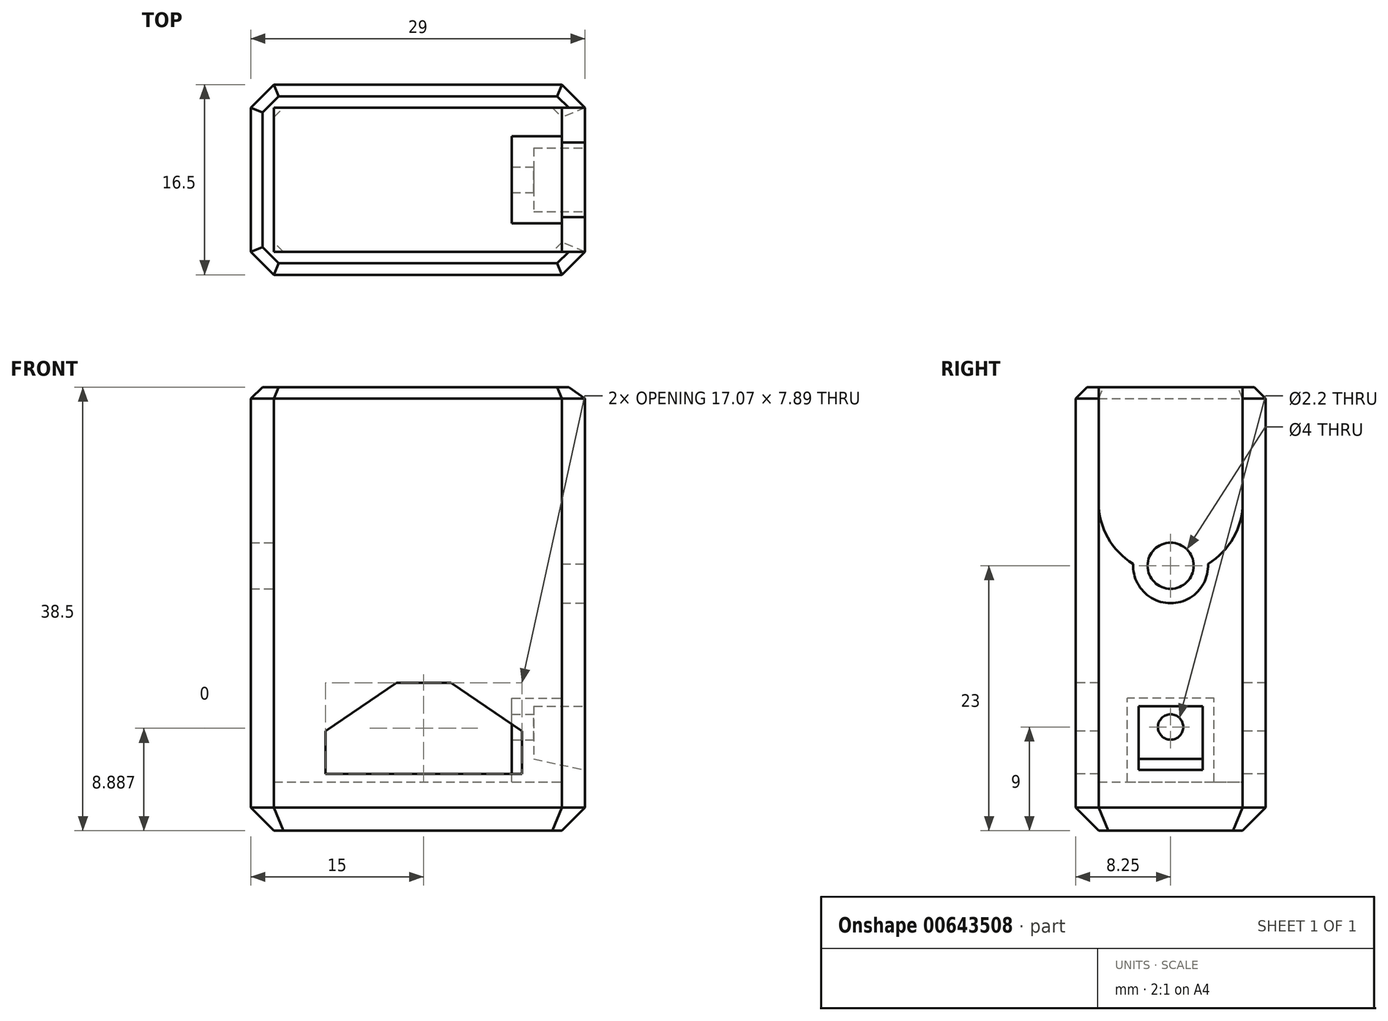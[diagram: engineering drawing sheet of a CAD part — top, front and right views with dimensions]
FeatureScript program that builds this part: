
annotation { "Feature Type Name" : "Feature", "Feature Type Description" : "" }
export const myFeature = defineFeature(function(context is Context, id is Id, definition is map)
    precondition{}
    {
        {
            var Q0;
            Q0=qCreatedBy(makeId("Top.planeOp"),FACE);
            var sketch = newSketch(context, id + "F0", { "sketchPlane" : qUnion([Q0])});
            skLineSegment(sketch, "E0.bottom", {"start": v(0, 0) * mm, "end": v(29, 0) * mm});
            skLineSegment(sketch, "E0.top", {"start": v(0, 16.5) * mm, "end": v(29, 16.5) * mm});
            skLineSegment(sketch, "E0.left", {"start": v(0, 0) * mm, "end": v(0, 16.5) * mm});
            skLineSegment(sketch, "E0.right", {"start": v(29, 0) * mm, "end": v(29, 16.5) * mm});
            skSolve(sketch);
        }
        {
            var Q0;
            Q0=qSketchRegion(id+"F0",true);
            extrude(context, id + "F1", {"entities" : qUnion([Q0]), "depth" : 38.5 * mm, "offsetDistance" : 25 * mm});
        }
        {
            var Q0;
            Q0=makeQuery(id+"F1.opExtrude","CAP_FACE",FACE,{"disambiguationData":[OSD([sQuery(id+"F0.wireOp",EDGE,"E0.bottom"),sQuery(id+"F0.wireOp",EDGE,"E0.top"),sQuery(id+"F0.wireOp",EDGE,"E0.left"),sQuery(id+"F0.wireOp",EDGE,"E0.right")])],"isStart":false});
            shell(context, id + "F2", {"entities" : qUnion([Q0]), "thickness" : 2 * mm});
        }
        {
            var Q0;
            Q0=makeQuery(id+"F2.opShell","OFFSET_FACE",FACE,{"disambiguationData":[OSD([sQuery(id+"F0.wireOp",EDGE,"E0.bottom"),sQuery(id+"F0.wireOp",EDGE,"E0.top"),sQuery(id+"F0.wireOp",EDGE,"E0.left"),sQuery(id+"F0.wireOp",EDGE,"E0.right")])]});
            extrude(context, id + "F3", {"entities" : qUnion([Q0]), "operationType" : NewBodyOperationType.ADD, "depth" : 2.25 * mm, "offsetDistance" : 25 * mm});
        }
        {
            var Q0;
            Q0=makeQuery(id+"F1.opExtrude","SWEPT_EDGE",EDGE,{"disambiguationData":[OSD([sQuery(id+"F0.wireOp",EDGE,"E0.bottom"),sQuery(id+"F0.wireOp",EDGE,"E0.right")])]});
            var Q1;
            Q1=makeQuery(id+"F1.opExtrude","SWEPT_EDGE",EDGE,{"disambiguationData":[OSD([sQuery(id+"F0.wireOp",EDGE,"E0.bottom"),sQuery(id+"F0.wireOp",EDGE,"E0.left")])]});
            var Q2;
            Q2=makeQuery(id+"F1.opExtrude","SWEPT_EDGE",EDGE,{"disambiguationData":[OSD([sQuery(id+"F0.wireOp",EDGE,"E0.top"),sQuery(id+"F0.wireOp",EDGE,"E0.right")])]});
            var Q3;
            Q3=makeQuery(id+"F1.opExtrude","SWEPT_EDGE",EDGE,{"disambiguationData":[OSD([sQuery(id+"F0.wireOp",EDGE,"E0.top"),sQuery(id+"F0.wireOp",EDGE,"E0.left")])]});
            chamfer(context, id + "F4", {"entities" : qUnion([Q0, Q1, Q2, Q3]), "width" : 2 * mm, "tangentPropagation" : true});
        }
        {
            var Q0;
            Q0=makeQuery(id+"F1.opExtrude","CAP_FACE",FACE,{"disambiguationData":[OSD([sQuery(id+"F0.wireOp",EDGE,"E0.bottom"),sQuery(id+"F0.wireOp",EDGE,"E0.top"),sQuery(id+"F0.wireOp",EDGE,"E0.left"),sQuery(id+"F0.wireOp",EDGE,"E0.right")])],"isStart":true});
            chamfer(context, id + "F5", {"entities" : qUnion([Q0]), "width" : 2 * mm, "tangentPropagation" : true});
        }
        {
            var Q0;
            Q0=makeQuery(id+"F1.opExtrude","CAP_EDGE",EDGE,{"disambiguationData":[OSD([sQuery(id+"F0.wireOp",EDGE,"E0.bottom")])],"isStart":false});
            var Q1;
            {var subQ0=sQuery(id+"F0.wireOp",EDGE,"E0.left");var subQ1=sQuery(id+"F0.wireOp",EDGE,"E0.bottom");Q1=makeQuery(id+"F4.opChamfer","BLEND_EDGE",EDGE,{"blendedFrom":[makeQuery(id+"F1.opExtrude","SWEPT_EDGE",EDGE,{"disambiguationData":[OSD([subQ1,subQ0])]}),makeQuery(id+"F1.opExtrude","CAP_FACE",FACE,{"disambiguationData":[OSD([subQ1,sQuery(id+"F0.wireOp",EDGE,"E0.top"),subQ0,sQuery(id+"F0.wireOp",EDGE,"E0.right")])],"isStart":false})],"blendedInto":[makeQuery(id+"F1.opExtrude","CAP_FACE",FACE,{"disambiguationData":[OSD([subQ1,sQuery(id+"F0.wireOp",EDGE,"E0.top"),subQ0,sQuery(id+"F0.wireOp",EDGE,"E0.right")])],"isStart":false})]});}
            var Q2;
            Q2=makeQuery(id+"F1.opExtrude","CAP_EDGE",EDGE,{"disambiguationData":[OSD([sQuery(id+"F0.wireOp",EDGE,"E0.left")])],"isStart":false});
            var Q3;
            {var subQ0=sQuery(id+"F0.wireOp",EDGE,"E0.left");var subQ1=sQuery(id+"F0.wireOp",EDGE,"E0.top");Q3=makeQuery(id+"F4.opChamfer","BLEND_EDGE",EDGE,{"blendedFrom":[makeQuery(id+"F1.opExtrude","SWEPT_EDGE",EDGE,{"disambiguationData":[OSD([subQ1,subQ0])]}),makeQuery(id+"F1.opExtrude","CAP_FACE",FACE,{"disambiguationData":[OSD([sQuery(id+"F0.wireOp",EDGE,"E0.bottom"),subQ1,subQ0,sQuery(id+"F0.wireOp",EDGE,"E0.right")])],"isStart":false})],"blendedInto":[makeQuery(id+"F1.opExtrude","CAP_FACE",FACE,{"disambiguationData":[OSD([sQuery(id+"F0.wireOp",EDGE,"E0.bottom"),subQ1,subQ0,sQuery(id+"F0.wireOp",EDGE,"E0.right")])],"isStart":false})]});}
            var Q4;
            Q4=makeQuery(id+"F1.opExtrude","CAP_EDGE",EDGE,{"disambiguationData":[OSD([sQuery(id+"F0.wireOp",EDGE,"E0.top")])],"isStart":false});
            var Q5;
            {var subQ0=sQuery(id+"F0.wireOp",EDGE,"E0.right");var subQ1=sQuery(id+"F0.wireOp",EDGE,"E0.top");Q5=makeQuery(id+"F4.opChamfer","BLEND_EDGE",EDGE,{"blendedFrom":[makeQuery(id+"F1.opExtrude","SWEPT_EDGE",EDGE,{"disambiguationData":[OSD([subQ1,subQ0])]}),makeQuery(id+"F1.opExtrude","CAP_FACE",FACE,{"disambiguationData":[OSD([sQuery(id+"F0.wireOp",EDGE,"E0.bottom"),subQ1,sQuery(id+"F0.wireOp",EDGE,"E0.left"),subQ0])],"isStart":false})],"blendedInto":[makeQuery(id+"F1.opExtrude","CAP_FACE",FACE,{"disambiguationData":[OSD([sQuery(id+"F0.wireOp",EDGE,"E0.bottom"),subQ1,sQuery(id+"F0.wireOp",EDGE,"E0.left"),subQ0])],"isStart":false})]});}
            var Q6;
            Q6=makeQuery(id+"F1.opExtrude","CAP_EDGE",EDGE,{"disambiguationData":[OSD([sQuery(id+"F0.wireOp",EDGE,"E0.right")])],"isStart":false});
            var Q7;
            {var subQ0=sQuery(id+"F0.wireOp",EDGE,"E0.right");var subQ1=sQuery(id+"F0.wireOp",EDGE,"E0.bottom");Q7=makeQuery(id+"F4.opChamfer","BLEND_EDGE",EDGE,{"blendedFrom":[makeQuery(id+"F1.opExtrude","SWEPT_EDGE",EDGE,{"disambiguationData":[OSD([subQ1,subQ0])]}),makeQuery(id+"F1.opExtrude","CAP_FACE",FACE,{"disambiguationData":[OSD([subQ1,sQuery(id+"F0.wireOp",EDGE,"E0.top"),sQuery(id+"F0.wireOp",EDGE,"E0.left"),subQ0])],"isStart":false})],"blendedInto":[makeQuery(id+"F1.opExtrude","CAP_FACE",FACE,{"disambiguationData":[OSD([subQ1,sQuery(id+"F0.wireOp",EDGE,"E0.top"),sQuery(id+"F0.wireOp",EDGE,"E0.left"),subQ0])],"isStart":false})]});}
            chamfer(context, id + "F6", {"entities" : qUnion([Q0, Q1, Q2, Q3, Q4, Q5, Q6, Q7]), "width" : 1 * mm, "tangentPropagation" : true});
        }
        {
            var Q0;
            Q0=makeQuery(id+"F1.opExtrude","SWEPT_FACE",FACE,{"disambiguationData":[OSD([sQuery(id+"F0.wireOp",EDGE,"E0.bottom")])]});
            var sketch = newSketch(context, id + "F7", { "sketchPlane" : qUnion([Q0])});
            skLineSegment(sketch, "E1", {"start": v(6.46, 4.94) * mm, "end": v(23.54, 4.94) * mm});
            skLineSegment(sketch, "E2", {"start": v(23.54, 4.94) * mm, "end": v(23.54, 8.66) * mm});
            skLineSegment(sketch, "E3", {"start": v(23.54, 8.66) * mm, "end": v(17.36, 12.83) * mm});
            skLineSegment(sketch, "E4", {"start": v(17.36, 12.83) * mm, "end": v(12.63, 12.83) * mm});
            skLineSegment(sketch, "E5", {"start": v(12.63, 12.83) * mm, "end": v(6.46, 8.66) * mm});
            skLineSegment(sketch, "E6", {"start": v(6.46, 8.66) * mm, "end": v(6.46, 4.94) * mm});
            skSolve(sketch);
        }
        {
            var Q0;
            Q0=makeQuery(id+"F7.imprint","IMPRINT",FACE,{"disambiguationData":[TD([[makeQuery(id+"F7.imprint","IMPRINT",EDGE,{"derivedFrom":sQuery(id+"F7.wireOp",EDGE,"E1")}),1.0]])]});
            extrude(context, id + "F8", {"entities" : qUnion([Q0]), "operationType" : NewBodyOperationType.REMOVE, "endBound" : BoundingType.THROUGH_ALL, "oppositeDirection" : true, "depth" : 25 * mm, "offsetDistance" : 25 * mm});
        }
        {
            var Q0;
            Q0=makeQuery(id+"F1.opExtrude","SWEPT_FACE",FACE,{"disambiguationData":[OSD([sQuery(id+"F0.wireOp",EDGE,"E0.right")])]});
            var sketch = newSketch(context, id + "F9", { "sketchPlane" : qUnion([Q0])});
            skCircle(sketch, "E7", {"center": v(8.25, 23) * mm, "radius": 3.25 * mm});
            skCircle(sketch, "E8", {"center": v(8.25, 28.5) * mm, "radius": 6.25 * mm});
            skLineSegment(sketch, "E9.bottom", {"start": v(2, 28.5) * mm, "end": v(14.5, 28.5) * mm});
            skLineSegment(sketch, "E9.top", {"start": v(2, 38.5) * mm, "end": v(14.5, 38.5) * mm});
            skLineSegment(sketch, "E9.left", {"start": v(2, 28.5) * mm, "end": v(2, 38.5) * mm});
            skLineSegment(sketch, "E9.right", {"start": v(14.5, 28.5) * mm, "end": v(14.5, 38.5) * mm});
            skSolve(sketch);
        }
        {
            var Q0;
            {var subQ0=sQuery(id+"F9.wireOp",EDGE,"E8");var subQ1=sQuery(id+"F9.wireOp",EDGE,"E7");var subQ2=makeQuery(id+"F9.imprint","INTERSECT",VERTEX,{"disambiguationData":[OD(0.0)],"derivedFrom":[subQ1,subQ0]});Q0=makeQuery(id+"F9.imprint","IMPRINT",FACE,{"disambiguationData":[TD([[makeQuery(id+"F9.imprint","IMPRINT",EDGE,{"disambiguationData":[TD([[subQ2,-1.0]])],"derivedFrom":subQ1}),1.0]])]});}
            var Q1;
            {var subQ0=sQuery(id+"F9.wireOp",EDGE,"E8");var subQ1=sQuery(id+"F9.wireOp",EDGE,"E7");var subQ2=makeQuery(id+"F9.imprint","INTERSECT",VERTEX,{"disambiguationData":[OD(0.0)],"derivedFrom":[subQ1,subQ0]});Q1=makeQuery(id+"F9.imprint","IMPRINT",FACE,{"disambiguationData":[TD([[makeQuery(id+"F9.imprint","IMPRINT",EDGE,{"disambiguationData":[TD([[subQ2,1.0]])],"derivedFrom":subQ1}),1.0]])]});}
            var Q2;
            {var subQ4=sQuery(id+"F9.wireOp",EDGE,"E9.bottom");Q2=makeQuery(id+"F9.imprint","IMPRINT",FACE,{"disambiguationData":[TD([[makeQuery(id+"F9.imprint","IMPRINT",EDGE,{"derivedFrom":subQ4}),-1.0]])]});}
            var Q3;
            {var subQ0=sQuery(id+"F9.wireOp",EDGE,"E9.bottom");Q3=makeQuery(id+"F9.imprint","IMPRINT",FACE,{"disambiguationData":[TD([[makeQuery(id+"F9.imprint","IMPRINT",EDGE,{"derivedFrom":subQ0}),1.0]])]});}
            var Q4;
            {var subQ3=sQuery(id+"F0.wireOp",EDGE,"E0.right");var subQ4=makeQuery(id+"F1.opExtrude","SWEPT_FACE",FACE,{"disambiguationData":[OSD([subQ3])]});var subQ8=makeQuery(id+"F6.opChamfer","BLEND_EDGE",EDGE,{"blendedFrom":[makeQuery(id+"F1.opExtrude","CAP_EDGE",EDGE,{"disambiguationData":[OSD([subQ3])],"isStart":false}),subQ4],"blendedInto":[subQ4]});Q4=makeQuery(id+"F9.imprint","IMPRINT",FACE,{"disambiguationData":[TD([[makeQuery(id+"F9.imprint","IMPRINT",EDGE,{"derivedFrom":subQ8}),1.0]])]});}
            var Q5;
            {var subQ0=sQuery(id+"F9.wireOp",EDGE,"E9.top");Q5=makeQuery(id+"F9.imprint","IMPRINT",FACE,{"disambiguationData":[TD([[makeQuery(id+"F9.imprint","IMPRINT",EDGE,{"derivedFrom":subQ0}),-1.0]])]});}
            extrude(context, id + "F10", {"entities" : qUnion([Q0, Q1, Q2, Q3, Q4, Q5]), "operationType" : NewBodyOperationType.REMOVE, "endBound" : BoundingType.UP_TO_NEXT, "oppositeDirection" : true, "depth" : 25 * mm, "offsetDistance" : 25 * mm});
        }
        {
            var Q0;
            Q0=makeQuery(id+"F2.opShell","OFFSET_FACE",FACE,{"disambiguationData":[OSD([sQuery(id+"F0.wireOp",EDGE,"E0.left")])]});
            var sketch = newSketch(context, id + "F11", { "sketchPlane" : qUnion([Q0])});
            skCircle(sketch, "E10", {"center": v(8.25, 23) * mm, "radius": 2 * mm});
            skSolve(sketch);
        }
        {
            var Q0;
            Q0=makeQuery(id+"F11.imprint","IMPRINT",FACE,{"disambiguationData":[TD([[makeQuery(id+"F11.imprint","IMPRINT",EDGE,{"derivedFrom":sQuery(id+"F11.wireOp",EDGE,"E10")}),1.0]])]});
            extrude(context, id + "F12", {"entities" : qUnion([Q0]), "operationType" : NewBodyOperationType.REMOVE, "endBound" : BoundingType.THROUGH_ALL, "oppositeDirection" : true, "depth" : 25 * mm, "offsetDistance" : 25 * mm});
        }
        {
            var Q0;
            Q0=makeQuery(id+"F2.opShell","OFFSET_FACE",FACE,{"disambiguationData":[OSD([sQuery(id+"F0.wireOp",EDGE,"E0.right")])]});
            var sketch = newSketch(context, id + "F13", { "sketchPlane" : qUnion([Q0])});
            skLineSegment(sketch, "E11.bottom", {"start": v(-12.02, 4.25) * mm, "end": v(-4.48, 4.25) * mm});
            skLineSegment(sketch, "E11.top", {"start": v(-12.02, 11.5) * mm, "end": v(-4.48, 11.5) * mm});
            skLineSegment(sketch, "E11.left", {"start": v(-12.02, 4.25) * mm, "end": v(-12.02, 11.5) * mm});
            skLineSegment(sketch, "E11.right", {"start": v(-4.48, 4.25) * mm, "end": v(-4.48, 11.5) * mm});
            skCircle(sketch, "E12", {"center": v(-8.25, 9) * mm, "radius": 1.1 * mm});
            skSolve(sketch);
        }
        {
            var Q0;
            Q0=qSketchRegion(id+"F13",true);
            extrude(context, id + "F14", {"entities" : qUnion([Q0]), "operationType" : NewBodyOperationType.ADD, "depth" : 4.35 * mm, "offsetDistance" : 25 * mm});
        }
        {
            var Q0;
            Q0=makeQuery(id+"F1.opExtrude","SWEPT_FACE",FACE,{"disambiguationData":[OSD([sQuery(id+"F0.wireOp",EDGE,"E0.right")])]});
            var sketch = newSketch(context, id + "F15", { "sketchPlane" : qUnion([Q0])});
            skLineSegment(sketch, "E13.bottom", {"start": v(5.48, 5.27) * mm, "end": v(11.02, 5.27) * mm});
            skLineSegment(sketch, "E13.top", {"start": v(5.48, 10.8) * mm, "end": v(11.02, 10.8) * mm});
            skLineSegment(sketch, "E13.left", {"start": v(5.48, 5.27) * mm, "end": v(5.48, 10.8) * mm});
            skLineSegment(sketch, "E13.right", {"start": v(11.02, 5.27) * mm, "end": v(11.02, 10.8) * mm});
            skSolve(sketch);
        }
        {
            var Q0;
            Q0=makeQuery(id+"F15.imprint","IMPRINT",FACE,{"disambiguationData":[TD([[makeQuery(id+"F15.imprint","IMPRINT",EDGE,{"derivedFrom":sQuery(id+"F15.wireOp",EDGE,"E13.bottom")}),-1.0]])]});
            cPlane(context, id + "F16", {"entities" : qUnion([Q0]), "cplaneType" : CPlaneType.OFFSET, "offset" : 4.45 * mm, "oppositeDirection" : true, "width" : 150 * mm, "height" : 150 * mm});
        }
        {
            var Q0;
            Q0=qCreatedBy(id+"F16.planeOp",FACE);
            var sketch = newSketch(context, id + "F17", { "sketchPlane" : qUnion([Q0])});
            skLineSegment(sketch, "E14.bottom", {"start": v(11.02, 10.8) * mm, "end": v(5.48, 10.8) * mm});
            skLineSegment(sketch, "E14.top", {"start": v(11.02, 6.22) * mm, "end": v(5.48, 6.22) * mm});
            skLineSegment(sketch, "E14.left", {"start": v(11.02, 10.8) * mm, "end": v(11.02, 6.22) * mm});
            skLineSegment(sketch, "E14.right", {"start": v(5.48, 10.8) * mm, "end": v(5.48, 6.22) * mm});
            skSolve(sketch);
        }
        {
            var Q1;
            Q1=qSketchRegion(id+"F17",true);
            var Q2;
            Q2=qSketchRegion(id+"F15",true);
            loft(context, id + "F18", {"operationType" : NewBodyOperationType.REMOVE, "sheetProfilesArray" : [{ "sheetProfileEntities" : qUnion([Q1]) }, { "sheetProfileEntities" : qUnion([Q2]) }]});
        }
    });
